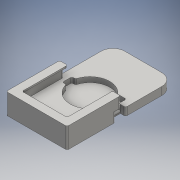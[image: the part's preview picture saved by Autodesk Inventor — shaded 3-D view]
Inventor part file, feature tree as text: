
AUTODESK INVENTOR PART (.ipt)
format: ipt  version: 2016 (Build 200138000, 138)  size: 312,320 bytes
history: native  units: mm
features: fillet x8, extrude x5, sketch x5
ambient origin geometry x8: Origin, YZ Plane, XZ Plane, XY Plane, X Axis, Y Axis, Z Axis, Center Point
bodies: Solid1 (feature_tree)
feature tree (18):
  extrude  "Extrusion1"  Depth=130.0mm
  extrude  "Extrusion2"  Depth=130.0mm
  extrude  "Extrusion3"  Depth=130.0mm
  extrude  "Extrusion4"  Depth=10.0mm TaperAngle=0.0deg
  extrude  "Extrusion5"  Depth=125.0mm
  fillet  "Fillet2"  Radius=13.0mm
  fillet  "Fillet3"  Radius=50.0mm
  fillet  "Fillet4"  Radius=6.0mm
  fillet  "Fillet6"  Radius=6.0mm
  fillet  "Fillet7"  Radius=61.5mm
  fillet  "Fillet8"  Radius=9.5mm
  fillet  "Fillet9"  Radius=2.0mm
  fillet  "Fillet10"  Radius=7.0mm
  sketch  "Sketch1"  dims[d0=67.0mm d1=130.0mm]
  sketch  "Sketch2"  dims[d2=5.0mm d3=130.0mm]
  sketch  "Sketch3"  dims[d4=5.0mm d5=130.0mm]
  sketch  "Sketch4"  dims[d6=5.0mm d7=10.0mm d8=0.0mm]
  sketch  "Sketch5"  dims[d9=67.0mm d10=125.0mm d11=13.0mm d12=0.0mm d13=50.0mm d15=6.0mm d16=6.0mm d17=61.5mm d18=9.5mm d19=2.0mm d20=7.0mm d23=25.0mm d24=25.0mm d26=62.769322mm d27=62.769322mm d28=4.5mm d29=2.0mm d30=4.5mm d31=2.0mm d32=8.5mm d33=51.5mm d34=83.5mm d35=2.0mm d36=2.0mm d37=6.5mm d38=0.0mm d39=70.0mm d40=6.5mm d41=0.0mm d42=9.0mm d43=3.5mm d44=3.5mm d45=5.5mm d46=5.5mm d47=3.5mm d48=10.0mm d49=10.0mm d50=10.0mm d51=3.0mm d52=0.0mm d54=2.0mm d55=2.0mm d56=15.0mm d58=2.0mm d59=1.0mm d60=1.0mm d61=1.0mm d62=1.0mm]
